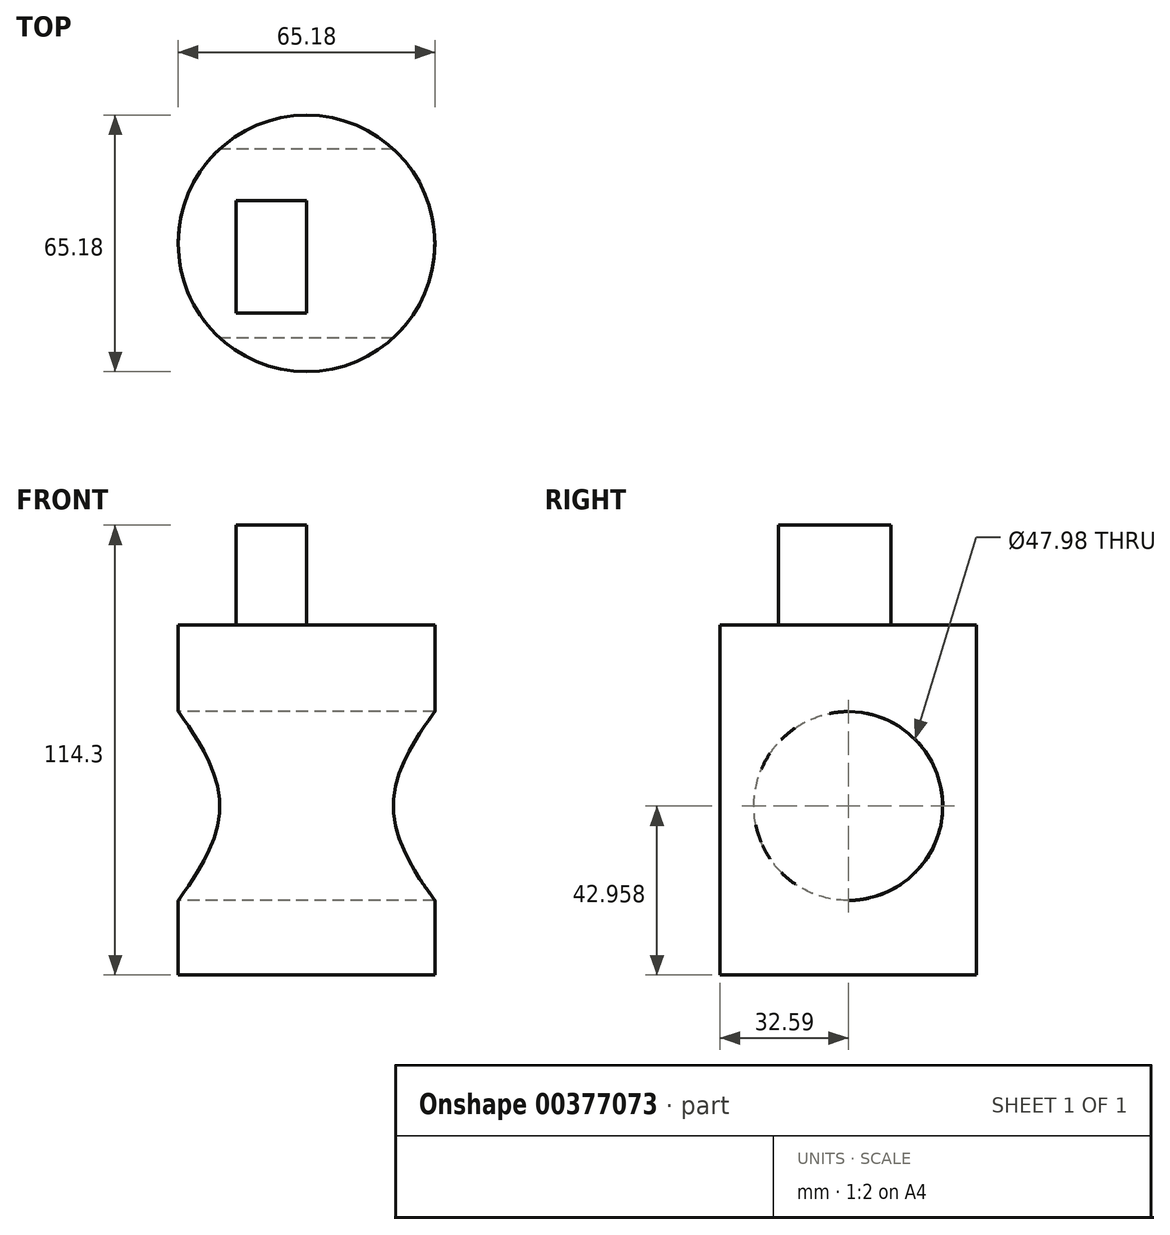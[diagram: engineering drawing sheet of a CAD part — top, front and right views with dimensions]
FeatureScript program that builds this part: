
annotation { "Feature Type Name" : "Feature", "Feature Type Description" : "" }
export const myFeature = defineFeature(function(context is Context, id is Id, definition is map)
    precondition{}
    {
        {
            var Q0;
            Q0=qCreatedBy(makeId("Top.planeOp"),FACE);
            var sketch = newSketch(context, id + "F0", { "sketchPlane" : qUnion([Q0])});
            skCircle(sketch, "E0", {"center": v(0, 0) * mm, "radius": 32.59 * mm});
            skSolve(sketch);
        }
        {
            var Q0;
            Q0 = qSketchRegion(id + "F0", true);
            extrude(context, id + "F1", {"entities" : qUnion([Q0]), "depth" : 88.9 * mm});
        }
        {
            var Q0;
            Q0=makeQuery(id+"F1.opExtrude","CAP_FACE",FACE,{"disambiguationData":[OSD([sQuery(id+"F0.wireOp",EDGE,"E0")])],"isStart":false});
            var sketch = newSketch(context, id + "F2", { "sketchPlane" : qUnion([Q0])});
            skLineSegment(sketch, "E1.bottom", {"start": v(-17.89, 10.86) * mm, "end": v(0, 10.86) * mm});
            skLineSegment(sketch, "E1.top", {"start": v(-17.89, -17.73) * mm, "end": v(0, -17.73) * mm});
            skLineSegment(sketch, "E1.left", {"start": v(-17.89, 10.86) * mm, "end": v(-17.89, -17.73) * mm});
            skLineSegment(sketch, "E1.right", {"start": v(0, 10.86) * mm, "end": v(0, -17.73) * mm});
            skSolve(sketch);
        }
        {
            var Q0;
            Q0 = qSketchRegion(id + "F2", true);
            extrude(context, id + "F3", {"entities" : qUnion([Q0]), "operationType" : NewBodyOperationType.ADD, "depth" : 25.4 * mm});
        }
        {
            var Q0;
            Q0=qCreatedBy(makeId("Right.planeOp"),FACE);
            var sketch = newSketch(context, id + "F4", { "sketchPlane" : qUnion([Q0])});
            skCircle(sketch, "E2", {"center": v(0, 42.96) * mm, "radius": 24 * mm});
            skSolve(sketch);
        }
        {
            var Q0;
            Q0 = qSketchRegion(id + "F4", true);
            extrude(context, id + "F5", {"entities" : qUnion([Q0]), "operationType" : NewBodyOperationType.REMOVE, "endBound" : BoundingType.SYMMETRIC, "depth" : 85.1 * mm});
        }
    });
